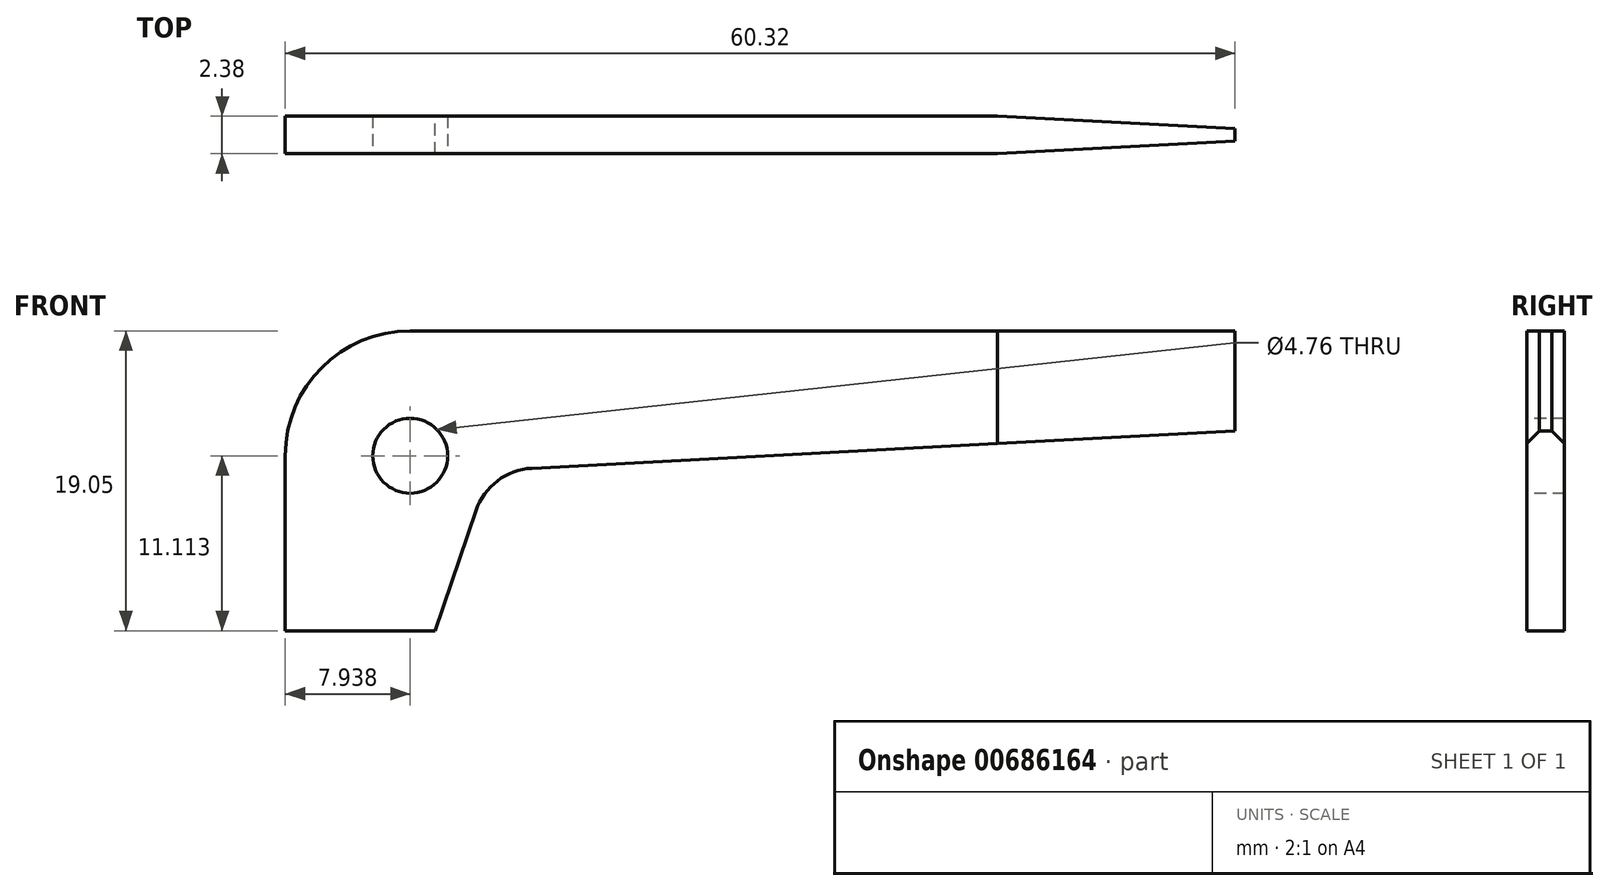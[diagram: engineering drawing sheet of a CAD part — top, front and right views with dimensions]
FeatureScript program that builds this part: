
annotation { "Feature Type Name" : "Feature", "Feature Type Description" : "" }
export const myFeature = defineFeature(function(context is Context, id is Id, definition is map)
    precondition{}
    {
        {
            var Q0;
            Q0=qCreatedBy(makeId("Front.planeOp"),FACE);
            var sketch = newSketch(context, id + "F0", { "sketchPlane" : qUnion([Q0])});
            skLineSegment(sketch, "E0.top", {"start": v(7.94, 19.05) * mm, "end": v(60.33, 19.05) * mm});
            skLineSegment(sketch, "E0.left", {"start": v(0, 0) * mm, "end": v(0, 11.11) * mm});
            skLineSegment(sketch, "E1", {"start": v(9.53, 0) * mm, "end": v(12.11, 7.63) * mm});
            skLineSegment(sketch, "E2", {"start": v(60.33, 12.7) * mm, "end": v(15.66, 10.32) * mm});
            skLineSegment(sketch, "E3", {"start": v(9.53, 0) * mm, "end": v(0, 0) * mm});
            skLineSegment(sketch, "E4", {"start": v(60.33, 12.7) * mm, "end": v(60.33, 19.05) * mm});
            skArc(sketch, "E5", {"start": v(15.66, 10.32) * mm, "mid": v(13.47, 9.52) * mm, "end": v(12.11, 7.63) * mm});
            skPoint(sketch, "E6.visualSharp", {"position": v(0, 19.05) * mm});
            skArc(sketch, "E6.filletArc", {"start": v(7.94, 19.05) * mm, "mid": v(2.32, 16.73) * mm, "end": v(0, 11.11) * mm});
            skSolve(sketch);
        }
        {
            var Q0;
            Q0 = qSketchRegion(id + "F0", true);
            extrude(context, id + "F1", {"entities" : qUnion([Q0]), "depth" : 2.38 * mm, "offsetDistance" : 25.4 * mm});
        }
        {
            var Q0;
            Q0=makeQuery(id+"F1.opExtrude","CAP_FACE",FACE,{"disambiguationData":[OSD([sQuery(id+"F0.wireOp",EDGE,"E0.top"),sQuery(id+"F0.wireOp",EDGE,"E0.left"),sQuery(id+"F0.wireOp",EDGE,"E1"),sQuery(id+"F0.wireOp",EDGE,"E2"),sQuery(id+"F0.wireOp",EDGE,"E3"),sQuery(id+"F0.wireOp",EDGE,"E4"),sQuery(id+"F0.wireOp",EDGE,"E5"),sQuery(id+"F0.wireOp",EDGE,"E6.filletArc")])],"isStart":false});
            var sketch = newSketch(context, id + "F2", { "sketchPlane" : qUnion([Q0])});
            skCircle(sketch, "E7", {"center": v(7.94, 11.11) * mm, "radius": 2.38 * mm});
            skSolve(sketch);
        }
        {
            var Q0;
            Q0=makeQuery(id+"F2.imprint","IMPRINT",FACE,{"disambiguationData":[TD([[makeQuery(id+"F2.imprint","IMPRINT",EDGE,{"derivedFrom":sQuery(id+"F2.wireOp",EDGE,"E7")}),1.0]])]});
            extrude(context, id + "F3", {"entities" : qUnion([Q0]), "operationType" : NewBodyOperationType.REMOVE, "endBound" : BoundingType.THROUGH_ALL, "oppositeDirection" : true, "depth" : 25.4 * mm, "offsetDistance" : 25.4 * mm});
        }
        {
            var Q0;
            Q0=makeQuery(id+"F1.opExtrude","SWEPT_FACE",FACE,{"disambiguationData":[OSD([sQuery(id+"F0.wireOp",EDGE,"E0.top")])]});
            var sketch = newSketch(context, id + "F4", { "sketchPlane" : qUnion([Q0])});
            skLineSegment(sketch, "E8", {"start": v(45.24, 0) * mm, "end": v(60.33, -0.8) * mm});
            skLineSegment(sketch, "E9", {"start": v(60.33, -0.8) * mm, "end": v(60.33, 0) * mm});
            skLineSegment(sketch, "E10", {"start": v(60.33, 0) * mm, "end": v(45.24, 0) * mm});
            skLineSegment(sketch, "E11.MirrorCS", {"start": v(45.24, -2.38) * mm, "end": v(60.33, -1.59) * mm});
            skLineSegment(sketch, "E12.MirrorCS", {"start": v(60.33, -2.38) * mm, "end": v(45.24, -2.38) * mm});
            skLineSegment(sketch, "E13.MirrorCS", {"start": v(60.33, -1.59) * mm, "end": v(60.33, -2.38) * mm});
            skSolve(sketch);
        }
        {
            var Q0;
            Q0=makeQuery(id+"F4.imprint","IMPRINT",FACE,{"disambiguationData":[TD([[makeQuery(id+"F4.imprint","IMPRINT",EDGE,{"derivedFrom":sQuery(id+"F4.wireOp",EDGE,"E8")}),1.0]])]});
            var Q1;
            Q1=makeQuery(id+"F4.imprint","IMPRINT",FACE,{"disambiguationData":[TD([[makeQuery(id+"F4.imprint","IMPRINT",EDGE,{"derivedFrom":sQuery(id+"F4.wireOp",EDGE,"E11.MirrorCS")}),-1.0]])]});
            extrude(context, id + "F5", {"entities" : qUnion([Q0, Q1]), "operationType" : NewBodyOperationType.REMOVE, "oppositeDirection" : true, "depth" : 25.4 * mm, "offsetDistance" : 25.4 * mm});
        }
    });
